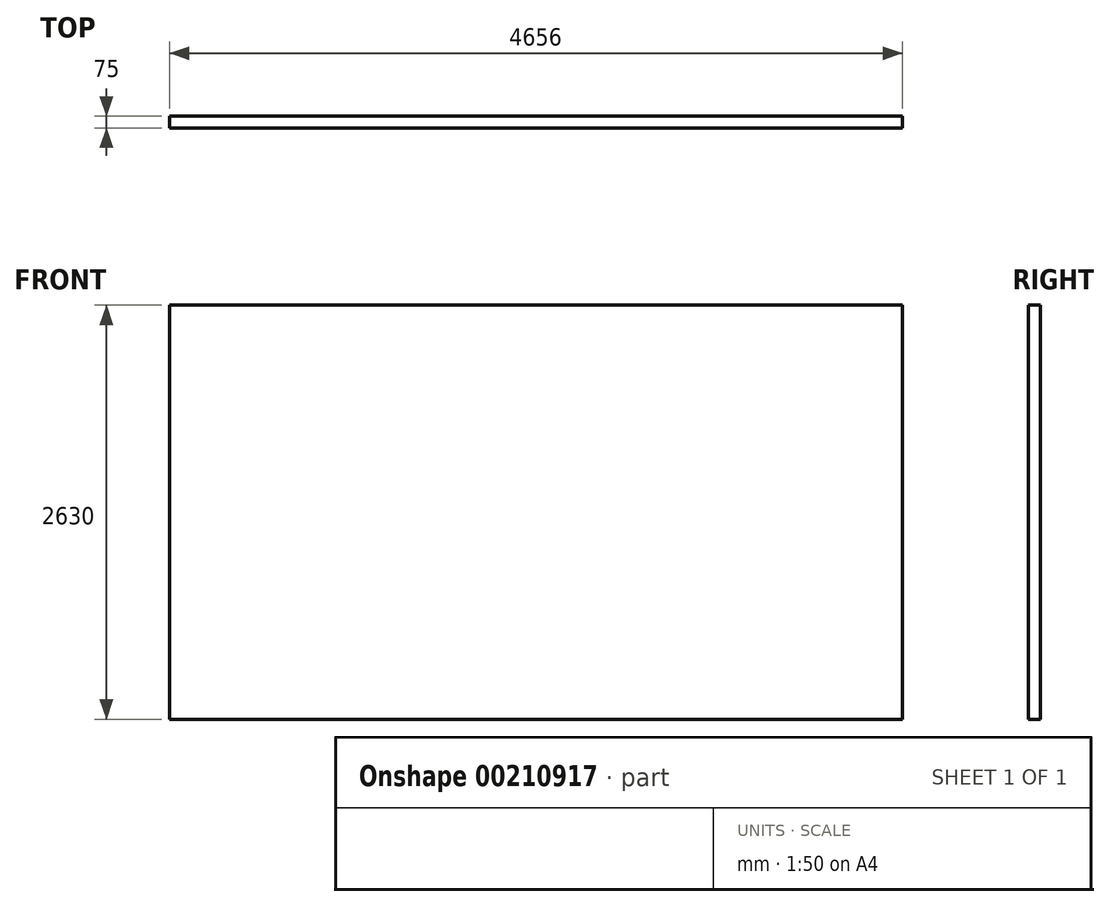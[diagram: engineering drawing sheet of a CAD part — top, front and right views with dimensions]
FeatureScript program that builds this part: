
annotation { "Feature Type Name" : "Feature", "Feature Type Description" : "" }
export const myFeature = defineFeature(function(context is Context, id is Id, definition is map)
    precondition{}
    {
        {
            var Q0;
            Q0=qCreatedBy(makeId("Front.planeOp"),FACE);
            var sketch = newSketch(context, id + "F0", { "sketchPlane" : qUnion([Q0])});
            skLineSegment(sketch, "E0.bottom", {"start": v(0, 0) * mm, "end": v(4656, 0) * mm});
            skLineSegment(sketch, "E0.right", {"start": v(4656, 0) * mm, "end": v(4656, 2630) * mm});
            skLineSegment(sketch, "E1", {"start": v(0, 2630) * mm, "end": v(4656, 2630) * mm});
            skLineSegment(sketch, "E2", {"start": v(0, 0) * mm, "end": v(0, 2630) * mm});
            skSolve(sketch);
        }
        {
            var Q0;
            Q0=makeQuery(id+"F0.imprint","IMPRINT",FACE,{"disambiguationData":[TD([[makeQuery(id+"F0.imprint","IMPRINT",EDGE,{"derivedFrom":sQuery(id+"F0.wireOp",EDGE,"E0.bottom")}),1.0]])]});
            extrude(context, id + "F1", {"entities" : qUnion([Q0]), "depth" : 75 * mm});
        }
    });
